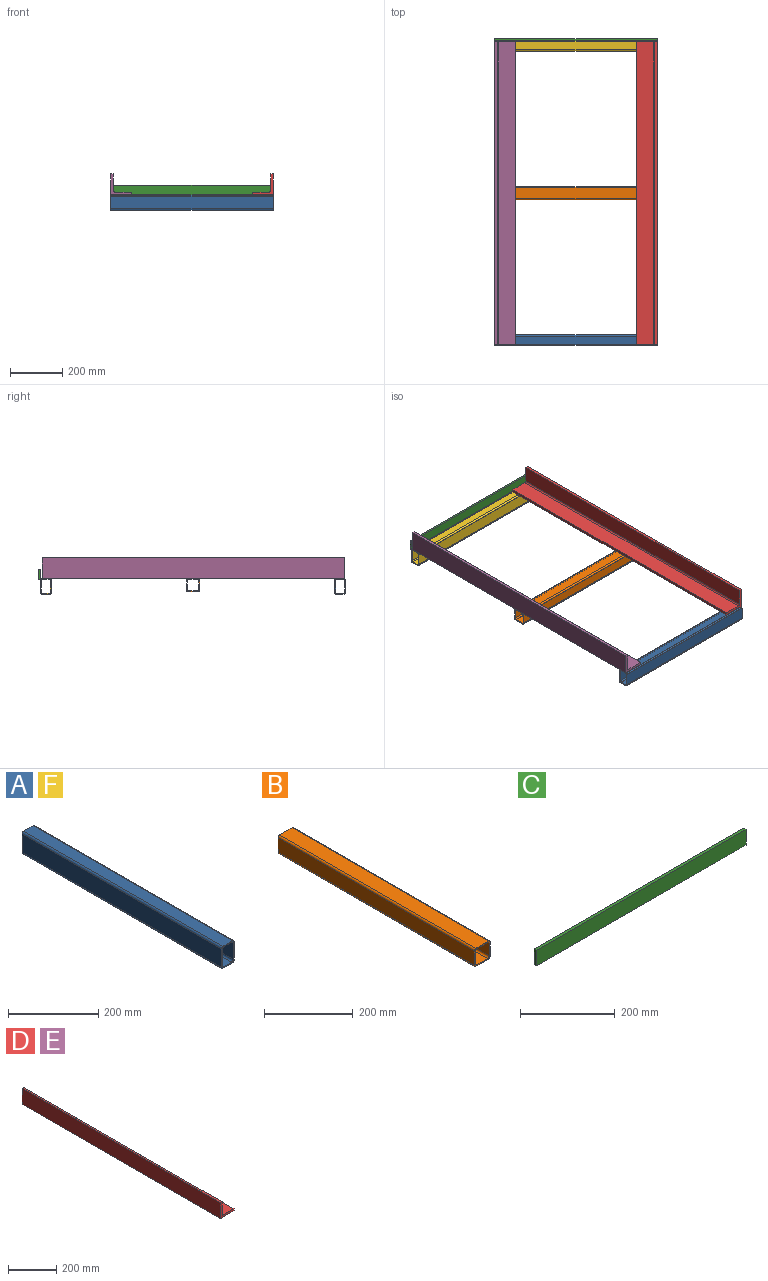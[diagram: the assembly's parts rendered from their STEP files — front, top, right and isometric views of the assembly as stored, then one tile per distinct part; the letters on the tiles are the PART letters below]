
ASSEMBLY  parts=6 mates=5
PART A: 18 faces, bbox 40x625x60 mm
  f0: plane 625x50mm, normal (1,0,0), area 31250mm2, adj f1,f15,f16,f17
  f1: cylinder r=5mm len=625mm, axis (0,1,0), area 4908.7mm2, adj f0,f2,f16,f17
  f2: plane 625x30mm, normal (0,0,1), area 18750mm2, adj f1,f3,f16,f17
  f3: cylinder r=5mm len=625mm, axis (0,1,0), area 4908.7mm2, adj f2,f4,f16,f17
  f4: plane 625x50mm, normal (-1,0,0), area 31250mm2, adj f3,f5,f16,f17
  f5: cylinder r=5mm len=625mm, axis (0,1,0), area 4908.7mm2, adj f4,f6,f16,f17
  f6: plane 625x30mm, normal (0,0,-1), area 18750mm2, adj f5,f15,f16,f17
  f7: cylinder r=5mm len=625mm, axis (0,1,0), area 4908.7mm2, adj f8,f14,f16,f17
  f8: plane 625x24.2mm, normal (0,0,1), area 15125mm2, adj f7,f9,f16,f17
  f9: cylinder r=5mm len=625mm, axis (0,1,0), area 4908.7mm2, adj f8,f10,f16,f17
  f10: plane 625x44.2mm, normal (1,0,0), area 27625mm2, adj f9,f11,f16,f17
  f11: cylinder r=5mm len=625mm, axis (0,1,0), area 4908.7mm2, adj f10,f12,f16,f17
  f12: plane 625x24.2mm, normal (0,0,-1), area 15125mm2, adj f11,f13,f16,f17
  f13: cylinder r=5mm len=625mm, axis (0,1,0), area 4908.7mm2, adj f12,f14,f16,f17
  f14: plane 625x44.2mm, normal (-1,0,0), area 27625mm2, adj f7,f13,f16,f17
  f15: cylinder r=5mm len=625mm, axis (0,1,0), area 4908.7mm2, adj f0,f6,f16,f17
  f16: plane 60x40mm, normal (0,-1,0), area 546.4mm2, adj f0,f1,f2,f3,f4,f5,f6,f7
  f17: plane 60x40mm, normal (0,1,0), area 546.4mm2, adj f0,f1,f2,f3,f4,f5,f6,f7
PART B: 18 faces, bbox 50x625x50 mm
  f0: plane 625x40mm, normal (1,0,0), area 25000mm2, adj f1,f15,f16,f17
  f1: cylinder r=5mm len=625mm, axis (0,1,0), area 4908.7mm2, adj f0,f2,f16,f17
  f2: plane 625x40mm, normal (0,0,1), area 25000mm2, adj f1,f3,f16,f17
  f3: cylinder r=5mm len=625mm, axis (0,1,0), area 4908.7mm2, adj f2,f4,f16,f17
  f4: plane 625x40mm, normal (-1,0,0), area 25000mm2, adj f3,f5,f16,f17
  f5: cylinder r=5mm len=625mm, axis (0,1,0), area 4908.7mm2, adj f4,f6,f16,f17
  f6: plane 625x40mm, normal (0,0,-1), area 25000mm2, adj f5,f15,f16,f17
  f7: cylinder r=5mm len=625mm, axis (0,1,0), area 4908.7mm2, adj f8,f14,f16,f17
  f8: plane 625x34mm, normal (-1,0,0), area 21250mm2, adj f7,f9,f16,f17
  f9: cylinder r=5mm len=625mm, axis (0,1,0), area 4908.7mm2, adj f8,f10,f16,f17
  f10: plane 625x34mm, normal (0,0,1), area 21250mm2, adj f9,f11,f16,f17
  f11: cylinder r=5mm len=625mm, axis (0,1,0), area 4908.7mm2, adj f10,f12,f16,f17
  f12: plane 625x34mm, normal (1,0,0), area 21250mm2, adj f11,f13,f16,f17
  f13: cylinder r=5mm len=625mm, axis (0,1,0), area 4908.7mm2, adj f12,f14,f16,f17
  f14: plane 625x34mm, normal (0,0,-1), area 21250mm2, adj f7,f13,f16,f17
  f15: cylinder r=5mm len=625mm, axis (0,1,0), area 4908.7mm2, adj f0,f6,f16,f17
  f16: plane 50x50mm, normal (0,-1,0), area 564mm2, adj f0,f1,f2,f3,f4,f5,f6,f7
  f17: plane 50x50mm, normal (0,1,0), area 564mm2, adj f0,f1,f2,f3,f4,f5,f6,f7
PART C: 6 faces, bbox 625x8x40 mm
  f0: plane 625x8mm, normal (0,0,-1), area 5000mm2, adj f1,f3,f4,f5
  f1: plane 40x8mm, normal (1,0,0), area 320mm2, adj f0,f2,f4,f5
  f2: plane 625x8mm, normal (0,0,1), area 5000mm2, adj f1,f3,f4,f5
  f3: plane 40x8mm, normal (-1,0,0), area 320mm2, adj f0,f2,f4,f5
  f4: plane 625x40mm, normal (0,-1,0), area 25000mm2, adj f0,f1,f2,f3
  f5: plane 625x40mm, normal (0,1,0), area 25000mm2, adj f0,f1,f2,f3
PART D: 9 faces, bbox 80x1160x80 mm
  f0: plane 1160x65mm, normal (1,0,0), area 75400mm2, adj f1,f6,f7,f8
  f1: plane 1160x10mm, normal (0,0,1), area 11600mm2, adj f0,f2,f7,f8
  f2: plane 1160x80mm, normal (-1,0,0), area 92800mm2, adj f1,f3,f7,f8
  f3: plane 1160x80mm, normal (0,0,-1), area 92800mm2, adj f2,f4,f7,f8
  f4: plane 1160x10mm, normal (1,0,0), area 11600mm2, adj f3,f5,f7,f8
  f5: plane 1160x65mm, normal (0,0,1), area 75400mm2, adj f4,f6,f7,f8
  f6: cylinder r=5mm len=1160mm, axis (0,1,0), area 9110.6mm2, adj f0,f5,f7,f8
  f7: plane 80x80mm, normal (0,-1,0), area 1505.4mm2, adj f0,f1,f2,f3,f4,f5,f6
  f8: plane 80x80mm, normal (0,1,0), area 1505.4mm2, adj f0,f1,f2,f3,f4,f5,f6
PART E: same geometry as D
PART F: same geometry as A
PLACE A rot(axis=(0,0,-1),90deg) t=(-267.3,-351.4,-120.64)mm
PLACE B rot(axis=(0,0,-1),90deg) t=(-267.3,213.6,-115.64)mm
PLACE C rot(axis=(0.1,-0.22,0.97),0deg) t=(-267.3,806.6,-75.64)mm
PLACE D rot(axis=(0,0,-1),180deg) t=(5.2,213.6,-50.64)mm
PLACE E rot(axis=(0,0,1),0deg) t=(-539.8,213.6,-50.64)mm
PLACE F rot(axis=(0,0,-1),90deg) t=(-267.3,778.6,-120.64)mm
MATE fastened C.f4 <-> F.f4  axis (0,-1,0) through (-267.3,798.6,-95.64)mm
MATE fastened F.f2 <-> E.f3  axis (0,0,1) through (-579.8,793.6,-90.64)mm
MATE fastened B.f2 <-> E.f3  axis (0,0,1) through (-579.8,213.6,-90.64)mm
MATE fastened A.f2 <-> D.f3  axis (0,0,1) through (45.2,-366.4,-90.64)mm
MATE fastened E.f3 <-> A.f2  axis (0,0,-1) through (-579.8,-366.4,-90.64)mm
